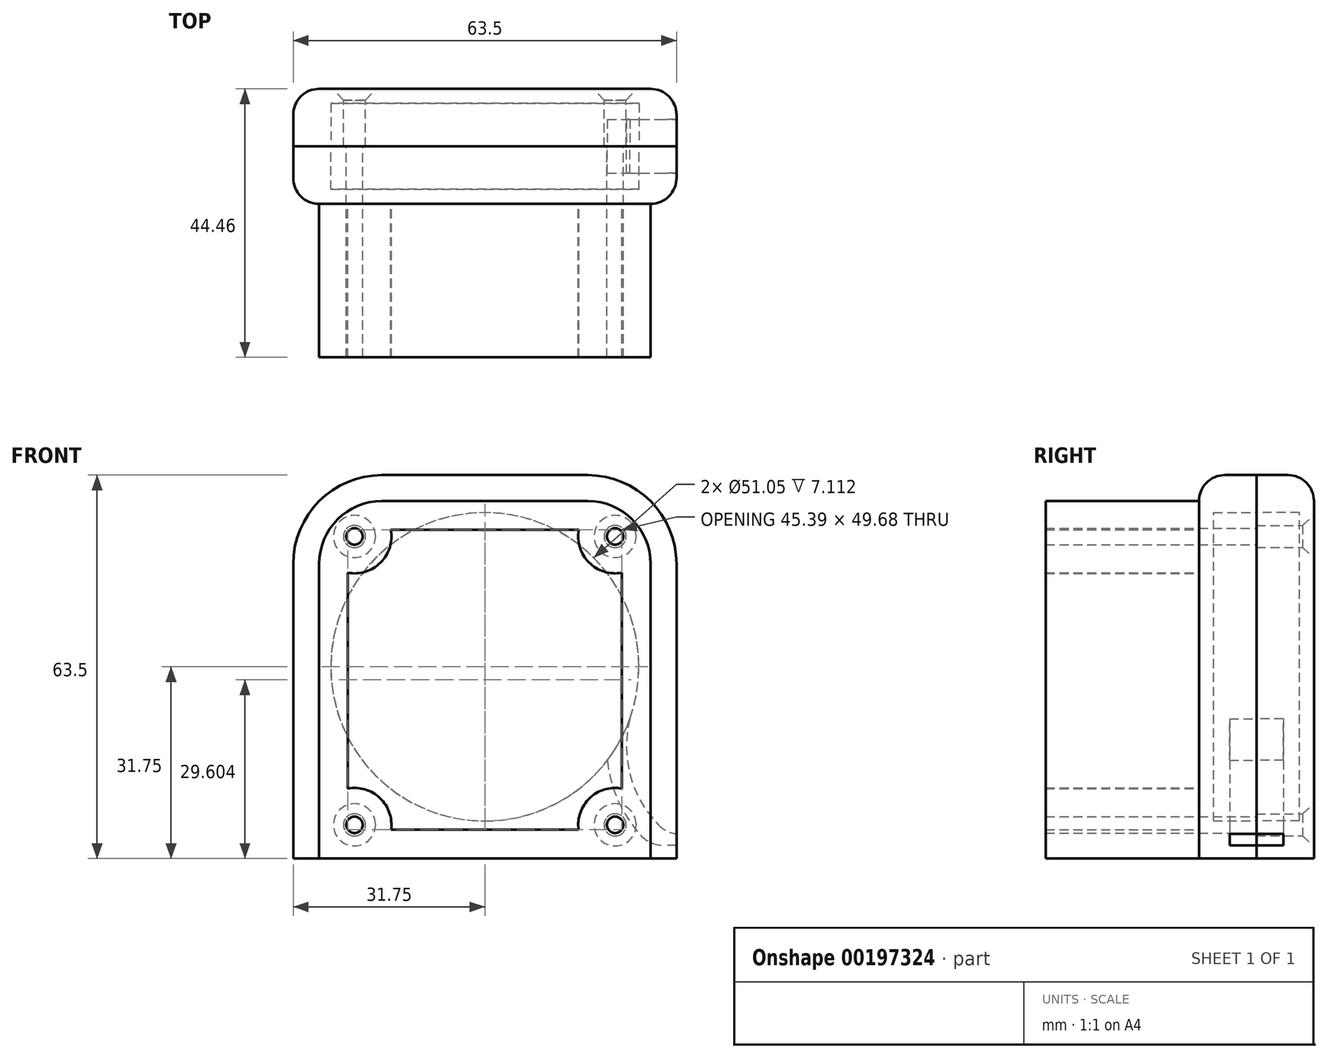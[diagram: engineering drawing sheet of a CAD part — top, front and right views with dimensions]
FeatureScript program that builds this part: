
annotation { "Feature Type Name" : "Feature", "Feature Type Description" : "" }
export const myFeature = defineFeature(function(context is Context, id is Id, definition is map)
    precondition{}
    {
        {
            var Q0;
            Q0=qCreatedBy(makeId("Front.planeOp"),FACE);
            var sketch = newSketch(context, id + "F0", { "sketchPlane" : qUnion([Q0])});
            skLineSegment(sketch, "E0.bottom", {"start": v(31.75, 31.75) * mm, "end": v(-31.75, 31.75) * mm});
            skLineSegment(sketch, "E0.top", {"start": v(31.75, -31.75) * mm, "end": v(-31.75, -31.75) * mm});
            skLineSegment(sketch, "E0.left", {"start": v(31.75, 31.75) * mm, "end": v(31.75, -31.75) * mm});
            skLineSegment(sketch, "E0.right", {"start": v(-31.75, 31.75) * mm, "end": v(-31.75, -31.75) * mm});
            skPoint(sketch, "E0.middle", {"position": v(0, 0) * mm});
            skSolve(sketch);
        }
        {
            var Q0;
            Q0 = qSketchRegion(id + "F0", true);
            extrude(context, id + "F1", {"entities" : qUnion([Q0]), "oppositeDirection" : true, "depth" : 9.52 * mm});
        }
        {
            var Q0;
            Q0=makeQuery(id+"F1.opExtrude","CAP_FACE",FACE,{"disambiguationData":[OSD([sQuery(id+"F0.wireOp",EDGE,"E0.bottom"),sQuery(id+"F0.wireOp",EDGE,"E0.top"),sQuery(id+"F0.wireOp",EDGE,"E0.left"),sQuery(id+"F0.wireOp",EDGE,"E0.right")])],"isStart":true});
            var sketch = newSketch(context, id + "F2", { "sketchPlane" : qUnion([Q0])});
            skCircle(sketch, "E1", {"center": v(0, 0) * mm, "radius": 25.53 * mm});
            skSolve(sketch);
        }
        {
            var Q0;
            Q0 = qSketchRegion(id + "F2", true);
            extrude(context, id + "F3", {"entities" : qUnion([Q0]), "operationType" : NewBodyOperationType.REMOVE, "oppositeDirection" : true, "depth" : 7.11 * mm});
        }
        {
            var Q0;
            Q0=makeQuery(id+"F1.opExtrude","CAP_FACE",FACE,{"disambiguationData":[OSD([sQuery(id+"F0.wireOp",EDGE,"E0.bottom"),sQuery(id+"F0.wireOp",EDGE,"E0.top"),sQuery(id+"F0.wireOp",EDGE,"E0.left"),sQuery(id+"F0.wireOp",EDGE,"E0.right")])],"isStart":true});
            var sketch = newSketch(context, id + "F4", { "sketchPlane" : qUnion([Q0])});
            skLineSegment(sketch, "E2.bottom", {"start": v(33.12, -29.55) * mm, "end": v(27.52, -29.55) * mm});
            skLineSegment(sketch, "E2.top", {"start": v(33.12, -27.65) * mm, "end": v(30.38, -27.65) * mm});
            skLineSegment(sketch, "E2.left", {"start": v(33.12, -29.55) * mm, "end": v(33.12, -27.65) * mm});
            skArc(sketch, "E3", {"start": v(24.03, -8.6) * mm, "mid": v(24.42, -19.05) * mm, "end": v(30.38, -27.65) * mm});
            skArc(sketch, "E4.0", {"start": v(20.29, -15.5) * mm, "mid": v(22.6, -23.2) * mm, "end": v(27.52, -29.55) * mm});
            skSolve(sketch);
        }
        {
            var Q0;
            {var subQ1=sQuery(id+"F4.wireOp",EDGE,"E3");Q0=makeQuery(id+"F4.imprint","IMPRINT",FACE,{"disambiguationData":[TD([[makeQuery(id+"F4.imprint","IMPRINT",EDGE,{"derivedFrom":subQ1}),-1.0]])]});}
            extrude(context, id + "F5", {"entities" : qUnion([Q0]), "operationType" : NewBodyOperationType.REMOVE, "oppositeDirection" : true, "depth" : 4.44 * mm});
        }
        {
            var Q0;
            Q0=makeQuery(id+"F5.boolean.opBoolean","COPY",EDGE,{"derivedFrom":makeQuery(id+"F5.opExtrude","SWEPT_EDGE",EDGE,{"disambiguationData":[OSD([sQuery(id+"F4.wireOp",EDGE,"E2.top"),sQuery(id+"F4.wireOp",EDGE,"E3")])]})});
            var Q1;
            Q1=makeQuery(id+"F5.boolean.opBoolean","COPY",EDGE,{"derivedFrom":makeQuery(id+"F5.opExtrude","SWEPT_EDGE",EDGE,{"disambiguationData":[OSD([sQuery(id+"F4.wireOp",EDGE,"E2.bottom"),sQuery(id+"F4.wireOp",EDGE,"E4.0")])]})});
            fillet(context, id + "F6", {"entities" : qUnion([Q0, Q1]), "radius" : 5.08 * mm, "tangentPropagation" : true, "allowEdgeOverflow" : false});
        }
        {
            var Q0;
            Q0=makeQuery(id+"F1.opExtrude","SWEPT_EDGE",EDGE,{"disambiguationData":[OSD([sQuery(id+"F0.wireOp",EDGE,"E0.bottom"),sQuery(id+"F0.wireOp",EDGE,"E0.left")])]});
            var Q1;
            Q1=makeQuery(id+"F1.opExtrude","SWEPT_EDGE",EDGE,{"disambiguationData":[OSD([sQuery(id+"F0.wireOp",EDGE,"E0.bottom"),sQuery(id+"F0.wireOp",EDGE,"E0.right")])]});
            fillet(context, id + "F7", {"entities" : qUnion([Q0, Q1]), "radius" : 14.72 * mm, "tangentPropagation" : true, "allowEdgeOverflow" : false});
        }
        {
            var Q0;
            Q0=makeQuery(id+"F1.opExtrude","CAP_EDGE",EDGE,{"disambiguationData":[OSD([sQuery(id+"F0.wireOp",EDGE,"E0.left")])],"isStart":false});
            fillet(context, id + "F8", {"entities" : qUnion([Q0]), "radius" : 4.3 * mm, "tangentPropagation" : true, "allowEdgeOverflow" : false});
        }
        {
            var Q0;
            Q0=makeQuery(id+"F1.opExtrude","CAP_FACE",FACE,{"disambiguationData":[OSD([sQuery(id+"F0.wireOp",EDGE,"E0.bottom"),sQuery(id+"F0.wireOp",EDGE,"E0.top"),sQuery(id+"F0.wireOp",EDGE,"E0.left"),sQuery(id+"F0.wireOp",EDGE,"E0.right")])],"isStart":false});
            var sketch = newSketch(context, id + "F9", { "sketchPlane" : qUnion([Q0])});
            skPoint(sketch, "E5", {"position": v(21.6, 21.59) * mm});
            skPoint(sketch, "E6", {"position": v(-21.6, 21.59) * mm});
            skPoint(sketch, "E7", {"position": v(21.6, -26.16) * mm});
            skPoint(sketch, "E8", {"position": v(-21.6, -26.16) * mm});
            skSolve(sketch);
        }
        {
            var Q0;
            Q0=sQuery(id+"F9.wireOp",VERTEX,"E5");
            var Q1;
            Q1=sQuery(id+"F9.wireOp",VERTEX,"E6");
            var Q2;
            Q2=sQuery(id+"F9.wireOp",VERTEX,"E8");
            var Q3;
            Q3=sQuery(id+"F9.wireOp",VERTEX,"E7");
            var Q4;
            Q4=makeQuery(id+"F1.opExtrude","SWEPT_BODY",BODY,{"disambiguationData":[OSD([sQuery(id+"F0.wireOp",EDGE,"E0.bottom"),sQuery(id+"F0.wireOp",EDGE,"E0.top"),sQuery(id+"F0.wireOp",EDGE,"E0.left"),sQuery(id+"F0.wireOp",EDGE,"E0.right")])]});
            hole(context, id + "F10", {"style" : HoleStyle.SIMPLE, "endStyle" : HoleEndStyle.THROUGH, "standardTappedOrClearance" : lookupTablePath({ "standard" : "ANSI", "engagement" : "75%", "pitch" : "32 tpi", "size" : "#6", "type" : "Tapped" }), "standardBlindInLast" : lookupTablePath({ "standard" : "ANSI", "engagement" : "75%", "pitch" : "32 tpi", "size" : "#6", "type" : "Tapped" }), "holeDiameter" : 2.7 * mm, "locations" : qUnion([Q0, Q1, Q2, Q3]), "scope" : qUnion([Q4]), "isTappedThrough" : true, "majorDiameter" : 3.5 * mm, "showTappedDepth" : true});
        }
        {
            var Q0;
            Q0=makeQuery(id+"F1.opExtrude","SWEPT_BODY",BODY,{"disambiguationData":[OSD([sQuery(id+"F0.wireOp",EDGE,"E0.bottom"),sQuery(id+"F0.wireOp",EDGE,"E0.top"),sQuery(id+"F0.wireOp",EDGE,"E0.left"),sQuery(id+"F0.wireOp",EDGE,"E0.right")])]});
            var Q1;
            Q1=makeQuery(id+"F1.opExtrude","CAP_FACE",FACE,{"disambiguationData":[OSD([sQuery(id+"F0.wireOp",EDGE,"E0.bottom"),sQuery(id+"F0.wireOp",EDGE,"E0.top"),sQuery(id+"F0.wireOp",EDGE,"E0.left"),sQuery(id+"F0.wireOp",EDGE,"E0.right")])],"isStart":true});
            mirror(context, id + "F11", {"entities" : qUnion([Q0]), "mirrorPlane" : qUnion([Q1])});
        }
        {
            var Q0;
            Q0=sQuery(id+"F9.wireOp",VERTEX,"E6");
            var Q1;
            Q1=sQuery(id+"F9.wireOp",VERTEX,"E5");
            var Q2;
            Q2=sQuery(id+"F9.wireOp",VERTEX,"E7");
            var Q3;
            Q3=sQuery(id+"F9.wireOp",VERTEX,"E8");
            var Q4;
            Q4=makeQuery(id+"F1.opExtrude","SWEPT_BODY",BODY,{"disambiguationData":[OSD([sQuery(id+"F0.wireOp",EDGE,"E0.bottom"),sQuery(id+"F0.wireOp",EDGE,"E0.top"),sQuery(id+"F0.wireOp",EDGE,"E0.left"),sQuery(id+"F0.wireOp",EDGE,"E0.right")])]});
            var Q5;
            Q5=makeQuery(id+"F11.opPattern","COPY",BODY,{"derivedFrom":makeQuery(id+"F1.opExtrude","SWEPT_BODY",BODY,{"disambiguationData":[OSD([sQuery(id+"F0.wireOp",EDGE,"E0.bottom"),sQuery(id+"F0.wireOp",EDGE,"E0.top"),sQuery(id+"F0.wireOp",EDGE,"E0.left"),sQuery(id+"F0.wireOp",EDGE,"E0.right")])]}),"instanceName":"1"});
            hole(context, id + "F12", {"style" : HoleStyle.C_SINK, "endStyle" : HoleEndStyle.BLIND_IN_LAST, "holeDiameter" : 3.66 * mm, "cSinkDiameter" : 7 * mm, "cSinkAngle" : 82 * degree, "tapDrillDiameter" : 2.7 * mm, "holeDepth" : 12.7 * mm, "locations" : qUnion([Q0, Q1, Q2, Q3]), "scope" : qUnion([Q4, Q5])});
        }
        {
            var Q0;
            Q0=makeQuery(id+"F11.opPattern","COPY",FACE,{"derivedFrom":makeQuery(id+"F1.opExtrude","CAP_FACE",FACE,{"disambiguationData":[OSD([sQuery(id+"F0.wireOp",EDGE,"E0.bottom"),sQuery(id+"F0.wireOp",EDGE,"E0.top"),sQuery(id+"F0.wireOp",EDGE,"E0.left"),sQuery(id+"F0.wireOp",EDGE,"E0.right")])],"isStart":false}),"instanceName":"1"});
            extrude(context, id + "F13", {"entities" : qUnion([Q0]), "depth" : 25.4 * mm});
        }
        {
            var Q0;
            Q0=makeQuery(id+"F13.opExtrude","CAP_FACE",FACE,{"disambiguationData":[OSD([sQuery(id+"F0.wireOp",EDGE,"E0.bottom"),sQuery(id+"F0.wireOp",EDGE,"E0.top"),sQuery(id+"F0.wireOp",EDGE,"E0.left"),sQuery(id+"F0.wireOp",EDGE,"E0.right")])],"isStart":false});
            var sketch = newSketch(context, id + "F14", { "sketchPlane" : qUnion([Q0])});
            skSolve(sketch);
        }
        {
            var Q0;
            Q0=makeQuery(id+"F13.opExtrude","CAP_FACE",FACE,{"disambiguationData":[OSD([sQuery(id+"F0.wireOp",EDGE,"E0.bottom"),sQuery(id+"F0.wireOp",EDGE,"E0.top"),sQuery(id+"F0.wireOp",EDGE,"E0.left"),sQuery(id+"F0.wireOp",EDGE,"E0.right")])],"isStart":false});
            var Q1;
            Q1=makeQuery(id+"F13.opExtrude","CAP_FACE",FACE,{"disambiguationData":[OSD([sQuery(id+"F0.wireOp",EDGE,"E0.bottom"),sQuery(id+"F0.wireOp",EDGE,"E0.top"),sQuery(id+"F0.wireOp",EDGE,"E0.left"),sQuery(id+"F0.wireOp",EDGE,"E0.right")])],"isStart":true});
            shell(context, id + "F15", {"entities" : qUnion([Q0, Q1]), "thickness" : 4.76 * mm});
        }
    });
